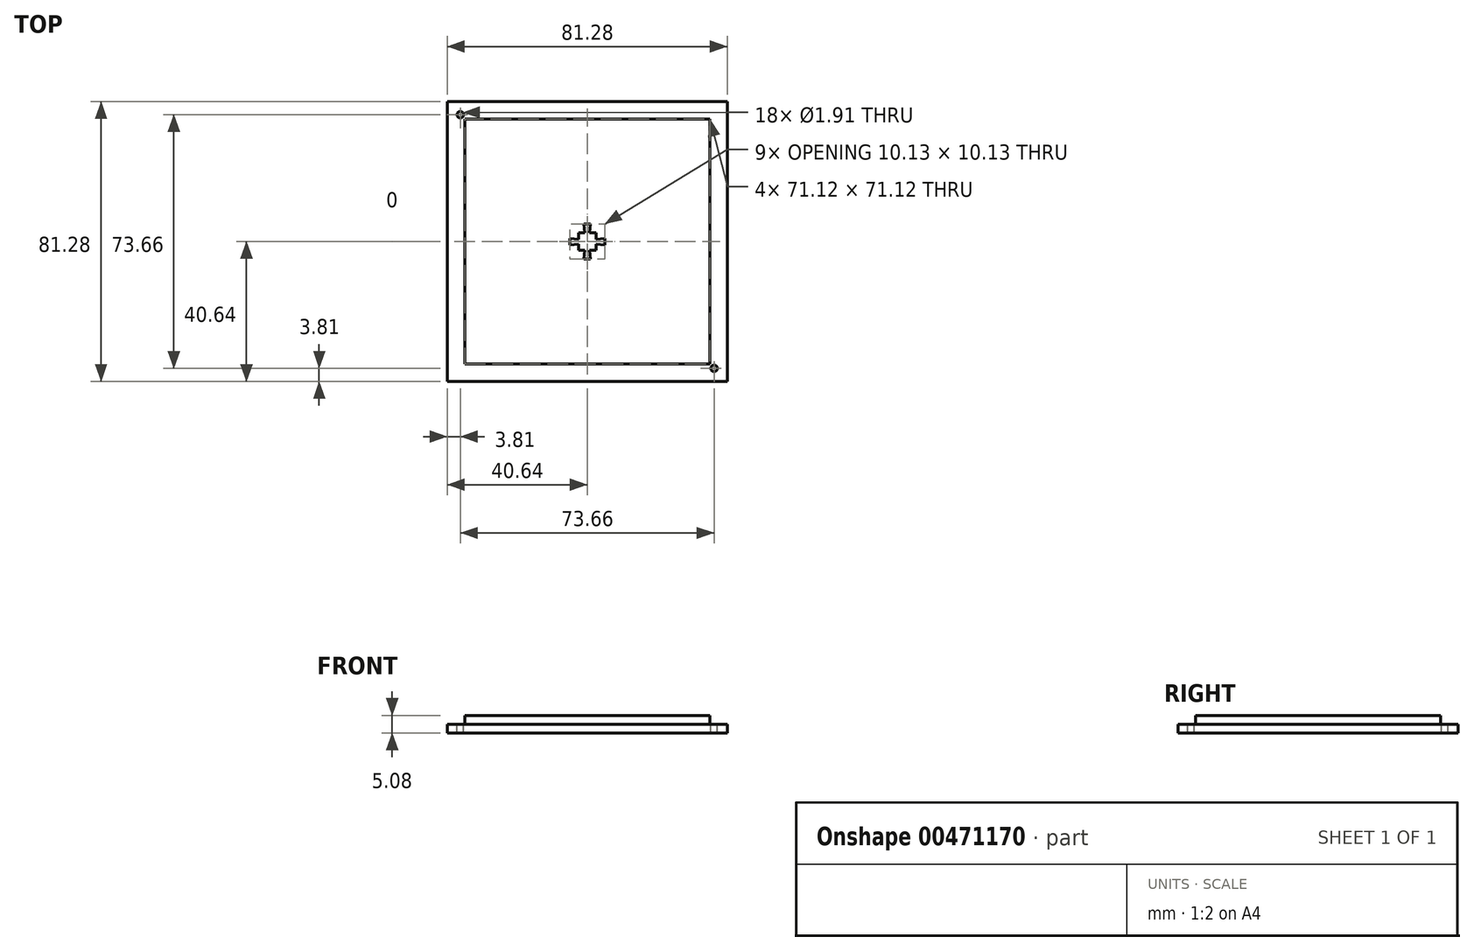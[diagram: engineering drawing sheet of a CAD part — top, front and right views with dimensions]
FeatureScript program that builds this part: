
annotation { "Feature Type Name" : "Feature", "Feature Type Description" : "" }
export const myFeature = defineFeature(function(context is Context, id is Id, definition is map)
    precondition{}
    {
        {
            var Q0;
            Q0=qCreatedBy(makeId("Top.planeOp"),FACE);
            var sketch = newSketch(context, id + "F0", { "sketchPlane" : qUnion([Q0])});
            skLineSegment(sketch, "E0.bottom", {"start": v(40.64, 40.64) * mm, "end": v(-40.64, 40.64) * mm});
            skLineSegment(sketch, "E0.top", {"start": v(40.64, -40.64) * mm, "end": v(-40.64, -40.64) * mm});
            skLineSegment(sketch, "E0.left", {"start": v(40.64, 40.64) * mm, "end": v(40.64, -40.64) * mm});
            skLineSegment(sketch, "E0.right", {"start": v(-40.64, 40.64) * mm, "end": v(-40.64, -40.64) * mm});
            skSolve(sketch);
        }
        {
            var Q0;
            Q0=qSketchRegion(id+"F0",true);
            extrude(context, id + "F1", {"entities" : qUnion([Q0]), "depth" : 38.1 * mm});
        }
        {
            var Q0;
            Q0=makeQuery(id+"F1.opExtrude","CAP_FACE",FACE,{"disambiguationData":[OSD([sQuery(id+"F0.wireOp",EDGE,"E0.bottom"),sQuery(id+"F0.wireOp",EDGE,"E0.top"),sQuery(id+"F0.wireOp",EDGE,"E0.left"),sQuery(id+"F0.wireOp",EDGE,"E0.right")])],"isStart":false});
            var sketch = newSketch(context, id + "F2", { "sketchPlane" : qUnion([Q0])});
            skLineSegment(sketch, "E1.bottom", {"start": v(35.56, 35.56) * mm, "end": v(-35.56, 35.56) * mm});
            skLineSegment(sketch, "E1.top", {"start": v(35.56, -35.56) * mm, "end": v(-35.56, -35.56) * mm});
            skLineSegment(sketch, "E1.left", {"start": v(35.56, 35.56) * mm, "end": v(35.56, -35.56) * mm});
            skLineSegment(sketch, "E1.right", {"start": v(-35.56, 35.56) * mm, "end": v(-35.56, -35.56) * mm});
            skSolve(sketch);
        }
        {
            var Q0;
            Q0=makeQuery(id+"F2.imprint","IMPRINT",FACE,{"disambiguationData":[TD([[makeQuery(id+"F2.imprint","IMPRINT",EDGE,{"derivedFrom":sQuery(id+"F2.wireOp",EDGE,"E1.bottom")}),-1.0]])]});
            extrude(context, id + "F3", {"entities" : qUnion([Q0]), "operationType" : NewBodyOperationType.REMOVE, "oppositeDirection" : true, "depth" : 35.56 * mm});
        }
        {
            var Q0;
            Q0=makeQuery(id+"F1.opExtrude","CAP_FACE",FACE,{"disambiguationData":[OSD([sQuery(id+"F0.wireOp",EDGE,"E0.bottom"),sQuery(id+"F0.wireOp",EDGE,"E0.top"),sQuery(id+"F0.wireOp",EDGE,"E0.left"),sQuery(id+"F0.wireOp",EDGE,"E0.right")])],"isStart":false});
            var sketch = newSketch(context, id + "F4", { "sketchPlane" : qUnion([Q0])});
            skLineSegment(sketch, "E2.bottom", {"start": v(38.1, 38.1) * mm, "end": v(-38.1, 38.1) * mm});
            skLineSegment(sketch, "E2.top", {"start": v(38.1, -38.1) * mm, "end": v(-38.1, -38.1) * mm});
            skLineSegment(sketch, "E2.left", {"start": v(38.1, 38.1) * mm, "end": v(38.1, -38.1) * mm});
            skLineSegment(sketch, "E2.right", {"start": v(-38.1, 38.1) * mm, "end": v(-38.1, -38.1) * mm});
            skSolve(sketch);
        }
        {
            var Q0;
            Q0 = qSketchRegion(id + "F4", true);
            extrude(context, id + "F5", {"entities" : qUnion([Q0]), "operationType" : NewBodyOperationType.REMOVE, "oppositeDirection" : true, "depth" : 33.02 * mm});
        }
        {
            var Q0;
            Q0=makeQuery(id+"F5.boolean.opBoolean","COPY",FACE,{"derivedFrom":makeQuery(id+"F5.opExtrude","CAP_FACE",FACE,{"disambiguationData":[OSD([sQuery(id+"F4.wireOp",EDGE,"E2.bottom"),sQuery(id+"F4.wireOp",EDGE,"E2.top"),sQuery(id+"F4.wireOp",EDGE,"E2.left"),sQuery(id+"F4.wireOp",EDGE,"E2.right")])],"isStart":false})});
            var sketch = newSketch(context, id + "F6", { "sketchPlane" : qUnion([Q0])});
            skLineSegment(sketch, "E3", {"start": v(0.95, -5.07) * mm, "end": v(-0.95, -5.07) * mm});
            skLineSegment(sketch, "E4", {"start": v(-0.95, -5.07) * mm, "end": v(-0.7, -2.54) * mm});
            skLineSegment(sketch, "E5", {"start": v(-0.7, -2.54) * mm, "end": v(-2.54, -2.54) * mm});
            skLineSegment(sketch, "E6", {"start": v(-2.54, -0.7) * mm, "end": v(-2.54, -2.54) * mm});
            skLineSegment(sketch, "E7", {"start": v(-2.54, -0.7) * mm, "end": v(-5.07, -0.95) * mm});
            skLineSegment(sketch, "E8", {"start": v(-5.07, 0.95) * mm, "end": v(-5.07, -0.95) * mm});
            skLineSegment(sketch, "E9", {"start": v(-5.07, 0.95) * mm, "end": v(-2.54, 0.7) * mm});
            skLineSegment(sketch, "E10", {"start": v(-2.54, 2.54) * mm, "end": v(-2.54, 0.7) * mm});
            skLineSegment(sketch, "E11", {"start": v(-2.54, 2.54) * mm, "end": v(-0.7, 2.54) * mm});
            skLineSegment(sketch, "E12", {"start": v(-0.95, 5.07) * mm, "end": v(-0.7, 2.54) * mm});
            skLineSegment(sketch, "E13", {"start": v(-0.95, 5.07) * mm, "end": v(0.95, 5.07) * mm});
            skLineSegment(sketch, "E14", {"start": v(0.95, 5.07) * mm, "end": v(0.7, 2.54) * mm});
            skLineSegment(sketch, "E15", {"start": v(0.7, 2.54) * mm, "end": v(2.54, 2.54) * mm});
            skLineSegment(sketch, "E16", {"start": v(2.54, 0.7) * mm, "end": v(2.54, 2.54) * mm});
            skLineSegment(sketch, "E17", {"start": v(2.54, 0.7) * mm, "end": v(5.07, 0.95) * mm});
            skLineSegment(sketch, "E18", {"start": v(5.07, -0.95) * mm, "end": v(5.07, 0.95) * mm});
            skLineSegment(sketch, "E19", {"start": v(5.07, -0.95) * mm, "end": v(2.54, -0.7) * mm});
            skLineSegment(sketch, "E20", {"start": v(2.54, -2.54) * mm, "end": v(2.54, -0.7) * mm});
            skLineSegment(sketch, "E21", {"start": v(2.54, -2.54) * mm, "end": v(0.7, -2.54) * mm});
            skLineSegment(sketch, "E22", {"start": v(0.7, -2.54) * mm, "end": v(0.95, -5.07) * mm});
            skSolve(sketch);
        }
        {
            var Q0;
            Q0 = qSketchRegion(id + "F6", true);
            extrude(context, id + "F7", {"entities" : qUnion([Q0]), "operationType" : NewBodyOperationType.REMOVE, "oppositeDirection" : true, "depth" : 25.4 * mm});
        }
        {
            var Q0;
            Q0=makeQuery(id+"F3.boolean.opBoolean","COPY",FACE,{"derivedFrom":makeQuery(id+"F3.opExtrude","CAP_FACE",FACE,{"disambiguationData":[OSD([sQuery(id+"F0.wireOp",EDGE,"E0.bottom"),sQuery(id+"F0.wireOp",EDGE,"E0.top"),sQuery(id+"F0.wireOp",EDGE,"E0.left"),sQuery(id+"F0.wireOp",EDGE,"E0.right"),sQuery(id+"F2.wireOp",EDGE,"E1.bottom"),sQuery(id+"F2.wireOp",EDGE,"E1.top"),sQuery(id+"F2.wireOp",EDGE,"E1.left"),sQuery(id+"F2.wireOp",EDGE,"E1.right")])],"isStart":false})});
            var sketch = newSketch(context, id + "F8", { "sketchPlane" : qUnion([Q0])});
            skCircle(sketch, "E23", {"center": v(-36.83, 36.83) * mm, "radius": 0.95 * mm});
            skPoint(sketch, "E24.orphan", {"position": v(-40.64, 40.64) * mm});
            skPoint(sketch, "E25.end.orphan", {"position": v(-35.56, 35.56) * mm});
            skSolve(sketch);
        }
        {
            var Q0;
            Q0 = qSketchRegion(id + "F8", true);
            extrude(context, id + "F9", {"entities" : qUnion([Q0]), "operationType" : NewBodyOperationType.REMOVE, "oppositeDirection" : true, "depth" : 25.4 * mm});
        }
        {
            var Q0;
            Q0=makeQuery(id+"F3.boolean.opBoolean","COPY",FACE,{"derivedFrom":makeQuery(id+"F3.opExtrude","CAP_FACE",FACE,{"disambiguationData":[OSD([sQuery(id+"F0.wireOp",EDGE,"E0.bottom"),sQuery(id+"F0.wireOp",EDGE,"E0.top"),sQuery(id+"F0.wireOp",EDGE,"E0.left"),sQuery(id+"F0.wireOp",EDGE,"E0.right"),sQuery(id+"F2.wireOp",EDGE,"E1.bottom"),sQuery(id+"F2.wireOp",EDGE,"E1.top"),sQuery(id+"F2.wireOp",EDGE,"E1.left"),sQuery(id+"F2.wireOp",EDGE,"E1.right")])],"isStart":false})});
            var sketch = newSketch(context, id + "F10", { "sketchPlane" : qUnion([Q0])});
            skCircle(sketch, "E26", {"center": v(36.83, -36.83) * mm, "radius": 0.95 * mm});
            skSolve(sketch);
        }
        {
            var Q0;
            Q0 = qSketchRegion(id + "F10", true);
            extrude(context, id + "F11", {"entities" : qUnion([Q0]), "operationType" : NewBodyOperationType.REMOVE, "oppositeDirection" : true, "depth" : 25.4 * mm});
        }
    });
